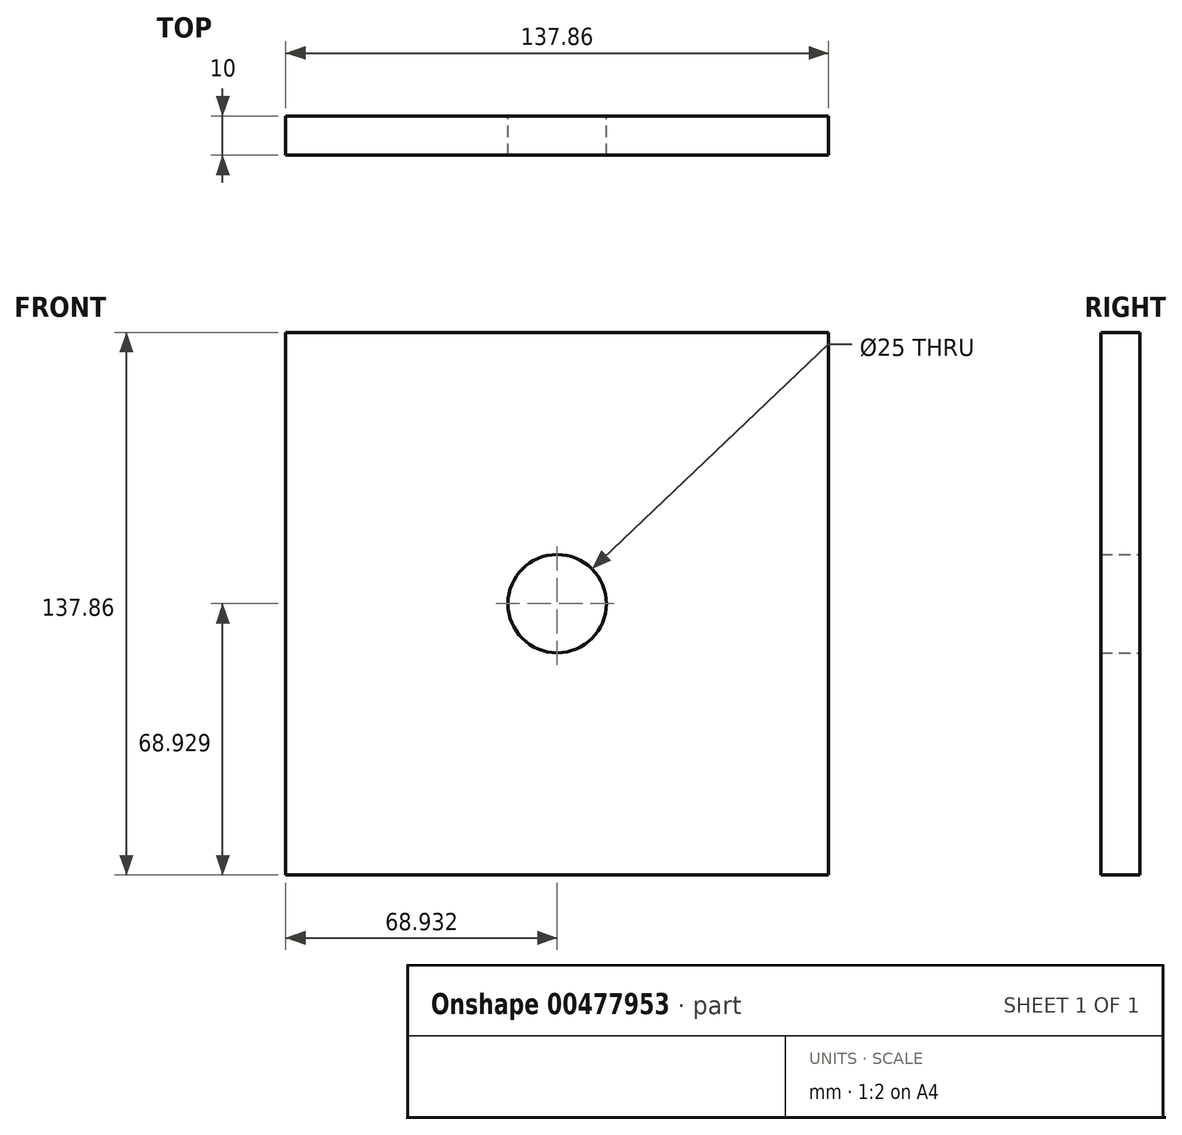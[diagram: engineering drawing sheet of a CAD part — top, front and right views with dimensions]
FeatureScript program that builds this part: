
annotation { "Feature Type Name" : "Feature", "Feature Type Description" : "" }
export const myFeature = defineFeature(function(context is Context, id is Id, definition is map)
    precondition{}
    {
        {
            var Q0;
            Q0=qCreatedBy(makeId("Front.planeOp"),FACE);
            var sketch = newSketch(context, id + "F0", { "sketchPlane" : qUnion([Q0])});
            skLineSegment(sketch, "E0.bottom", {"start": v(-87.64, 84.96) * mm, "end": v(50.22, 84.96) * mm});
            skLineSegment(sketch, "E0.top", {"start": v(-87.64, -52.9) * mm, "end": v(50.22, -52.9) * mm});
            skLineSegment(sketch, "E0.left", {"start": v(-87.64, 84.96) * mm, "end": v(-87.64, -52.9) * mm});
            skLineSegment(sketch, "E0.right", {"start": v(50.22, 84.96) * mm, "end": v(50.22, -52.9) * mm});
            skCircle(sketch, "E1", {"center": v(-18.7, 16.03) * mm, "radius": 12.5 * mm});
            skPoint(sketch, "E1.centerSnap0", {"position": v(-87.64, 16.03) * mm});
            skPoint(sketch, "E1.centerSnap1", {"position": v(-18.7, 84.96) * mm});
            skSolve(sketch);
        }
        {
            var Q0;
            Q0=makeQuery(id+"F0.imprint","IMPRINT",FACE,{"disambiguationData":[TD([[makeQuery(id+"F0.imprint","IMPRINT",EDGE,{"derivedFrom":sQuery(id+"F0.wireOp",EDGE,"E0.bottom")}),-1.0]])]});
            extrude(context, id + "F1", {"entities" : qUnion([Q0]), "depth" : 10 * mm, "offsetDistance" : 25 * mm});
        }
    });
